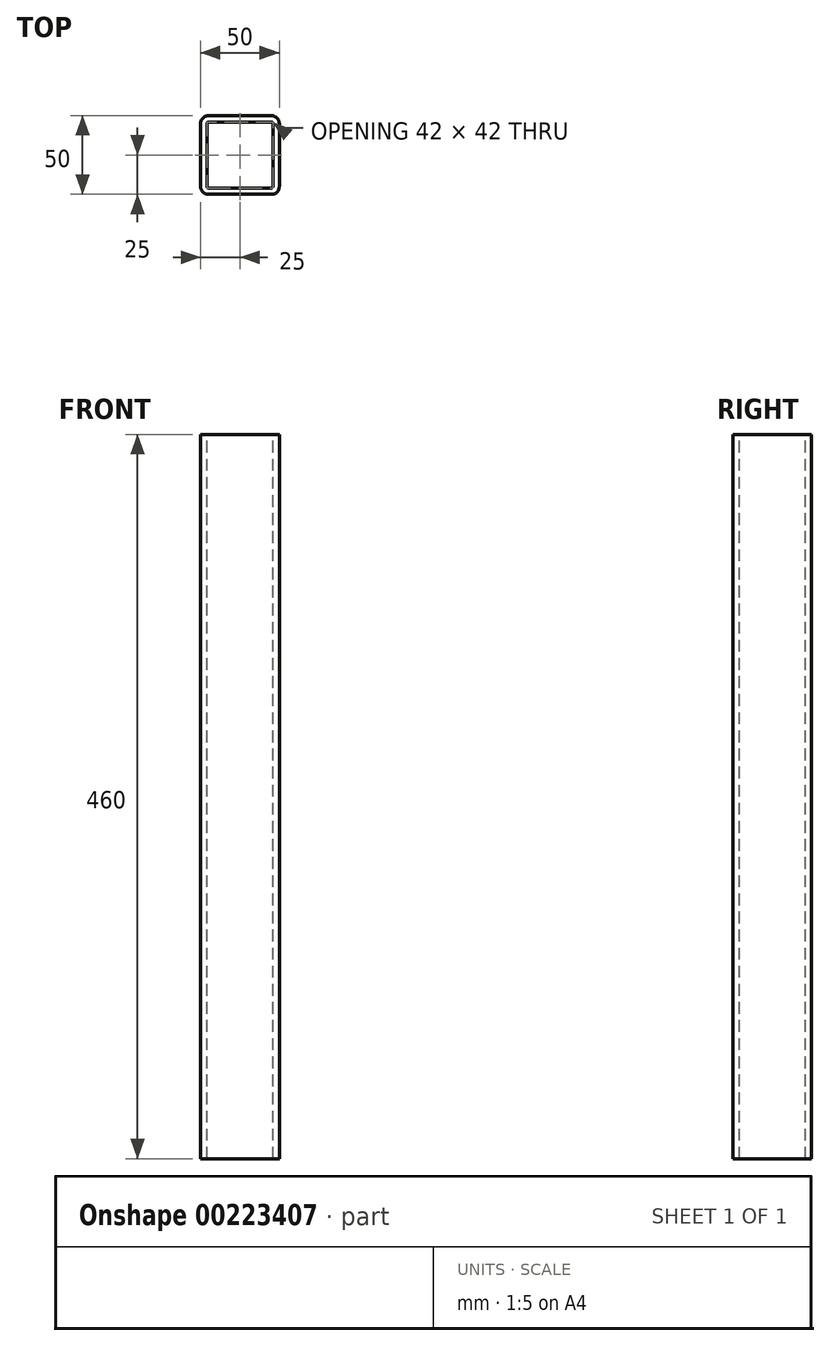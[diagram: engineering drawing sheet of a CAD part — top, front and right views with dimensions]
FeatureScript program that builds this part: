
annotation { "Feature Type Name" : "Feature", "Feature Type Description" : "" }
export const myFeature = defineFeature(function(context is Context, id is Id, definition is map)
    precondition{}
    {
        {
            var Q0;
            Q0=qCreatedBy(makeId("Top.planeOp"),FACE);
            var sketch = newSketch(context, id + "F0", { "sketchPlane" : qUnion([Q0])});
            skLineSegment(sketch, "E0.bottom", {"start": v(5, 0) * mm, "end": v(45, 0) * mm});
            skLineSegment(sketch, "E0.top", {"start": v(5, -50) * mm, "end": v(45, -50) * mm});
            skLineSegment(sketch, "E0.left", {"start": v(0, -5) * mm, "end": v(0, -45) * mm});
            skLineSegment(sketch, "E0.right", {"start": v(50, -5) * mm, "end": v(50, -45) * mm});
            skPoint(sketch, "E1.visualSharp", {"position": v(50, 0) * mm});
            skArc(sketch, "E1.filletArc", {"start": v(50, -5) * mm, "mid": v(48.54, -1.46) * mm, "end": v(45, 0) * mm});
            skPoint(sketch, "E2.visualSharp", {"position": v(50, -50) * mm});
            skArc(sketch, "E2.filletArc", {"start": v(45, -50) * mm, "mid": v(48.54, -48.54) * mm, "end": v(50, -45) * mm});
            skPoint(sketch, "E3.visualSharp", {"position": v(0, -50) * mm});
            skArc(sketch, "E3.filletArc", {"start": v(0, -45) * mm, "mid": v(1.46, -48.54) * mm, "end": v(5, -50) * mm});
            skPoint(sketch, "E4.visualSharp", {"position": v(0, 0) * mm});
            skArc(sketch, "E4.filletArc", {"start": v(5, 0) * mm, "mid": v(1.46, -1.46) * mm, "end": v(0, -5) * mm});
            skLineSegment(sketch, "E5.0", {"start": v(4, -5) * mm, "end": v(4, -45) * mm});
            skArc(sketch, "E5.1", {"start": v(5, -4) * mm, "mid": v(4.3, -4.3) * mm, "end": v(4, -5) * mm});
            skArc(sketch, "E5.2", {"start": v(4, -45) * mm, "mid": v(4.3, -45.7) * mm, "end": v(5, -46) * mm});
            skLineSegment(sketch, "E5.3", {"start": v(5, -4) * mm, "end": v(45, -4) * mm});
            skLineSegment(sketch, "E5.4", {"start": v(5, -46) * mm, "end": v(45, -46) * mm});
            skArc(sketch, "E5.5", {"start": v(45, -46) * mm, "mid": v(45.7, -45.7) * mm, "end": v(46, -45) * mm});
            skLineSegment(sketch, "E5.6", {"start": v(46, -5) * mm, "end": v(46, -45) * mm});
            skArc(sketch, "E5.7", {"start": v(46, -5) * mm, "mid": v(45.7, -4.3) * mm, "end": v(45, -4) * mm});
            skSolve(sketch);
        }
        {
            var Q0;
            Q0=makeQuery(id+"F0.imprint","IMPRINT",FACE,{"disambiguationData":[TD([[makeQuery(id+"F0.imprint","IMPRINT",EDGE,{"derivedFrom":sQuery(id+"F0.wireOp",EDGE,"E0.bottom")}),-1.0]])]});
            extrude(context, id + "F1", {"entities" : qUnion([Q0]), "oppositeDirection" : true, "depth" : 460 * mm});
        }
    });
